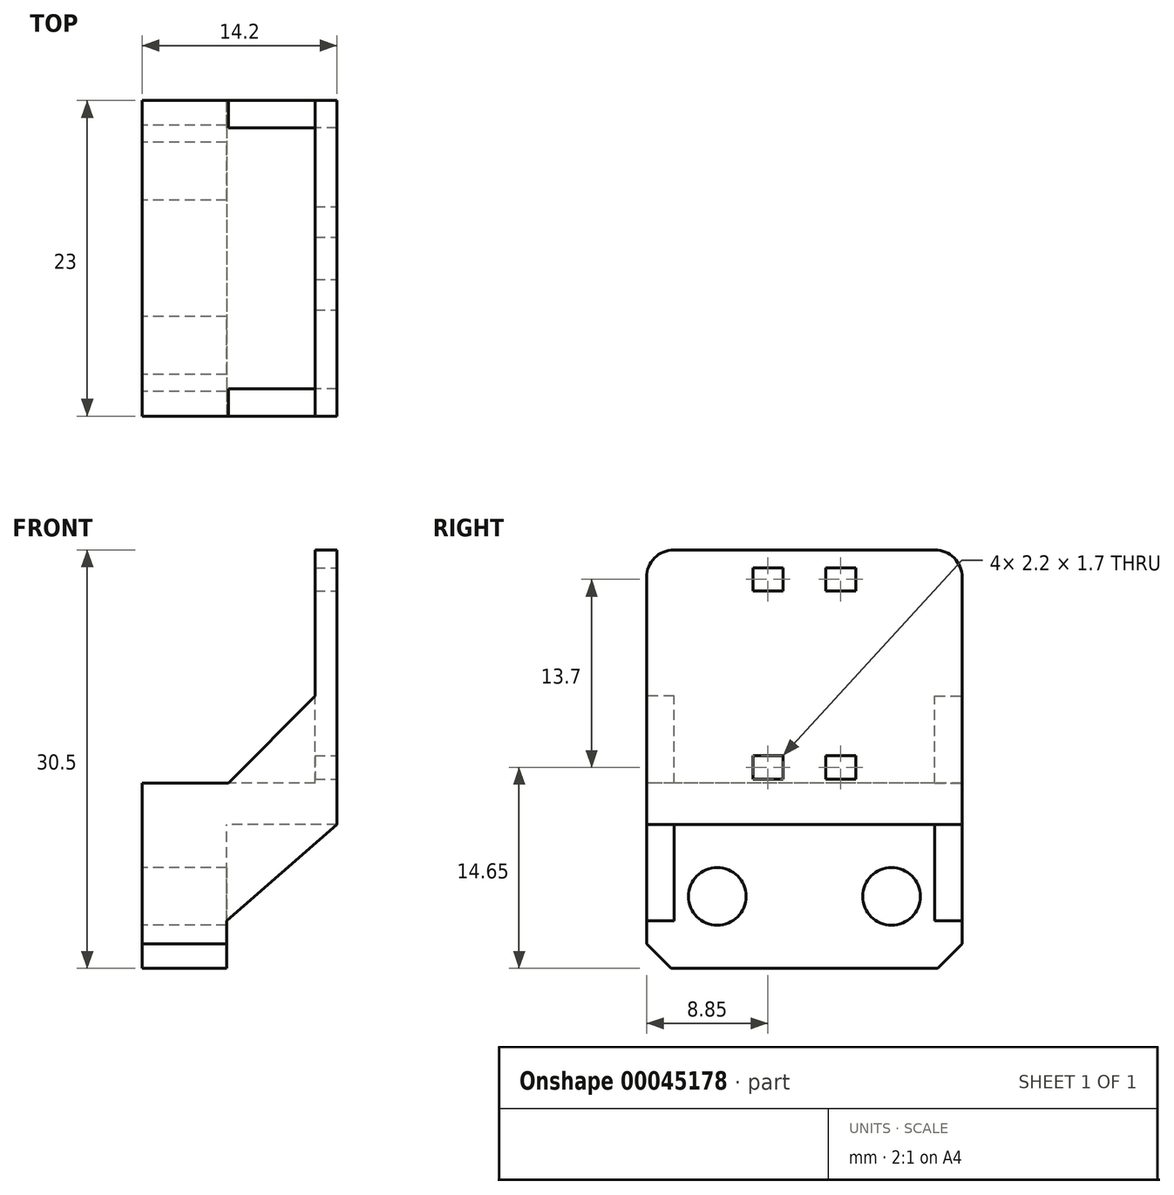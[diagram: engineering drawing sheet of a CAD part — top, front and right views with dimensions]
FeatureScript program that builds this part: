
annotation { "Feature Type Name" : "Feature", "Feature Type Description" : "" }
export const myFeature = defineFeature(function(context is Context, id is Id, definition is map)
    precondition{}
    {
        {
            var Q0;
            Q0=qCreatedBy(makeId("Right.planeOp"),FACE);
            var sketch = newSketch(context, id + "F0", { "sketchPlane" : qUnion([Q0])});
            skLineSegment(sketch, "E0.rect.bottom", {"start": v(9.71, -5.25) * mm, "end": v(-9.71, -5.25) * mm});
            skLineSegment(sketch, "E0.rect.top", {"start": v(9.71, 5.25) * mm, "end": v(-9.71, 5.25) * mm});
            skLineSegment(sketch, "E0.rect.left", {"start": v(11.5, -3.46) * mm, "end": v(11.5, 3.46) * mm});
            skLineSegment(sketch, "E0.rect.right", {"start": v(-11.5, -3.46) * mm, "end": v(-11.5, 3.46) * mm});
            skPoint(sketch, "E0.rect.middle", {"position": v(0, 0) * mm});
            skLineSegment(sketch, "E1", {"start": v(6.35, 5.25) * mm, "end": v(6.35, -5.25) * mm, "construction": true});
            skCircle(sketch, "E2", {"center": v(6.35, 0) * mm, "radius": 2.1 * mm});
            skCircle(sketch, "E3.MirrorC", {"center": v(-6.35, 0) * mm, "radius": 2.1 * mm});
            skLineSegment(sketch, "E4.MirrorCS", {"start": v(-9.71, -5.25) * mm, "end": v(-11.5, -3.46) * mm});
            skLineSegment(sketch, "E5.MirrorCS", {"start": v(9.71, -5.25) * mm, "end": v(11.5, -3.46) * mm});
            skPoint(sketch, "E6.orphan", {"position": v(-11.5, 5.25) * mm});
            skPoint(sketch, "E7.orphan", {"position": v(-11.5, -5.25) * mm});
            skPoint(sketch, "E8.orphan", {"position": v(11.5, 5.25) * mm});
            skPoint(sketch, "E9.orphan", {"position": v(11.5, -5.25) * mm});
            skLineSegment(sketch, "E10", {"start": v(11.5, 3.46) * mm, "end": v(11.5, 5.25) * mm});
            skLineSegment(sketch, "E11", {"start": v(11.5, 5.25) * mm, "end": v(9.71, 5.25) * mm});
            skLineSegment(sketch, "E12", {"start": v(-11.5, 3.46) * mm, "end": v(-11.5, 5.25) * mm});
            skLineSegment(sketch, "E13", {"start": v(-11.5, 5.25) * mm, "end": v(-9.71, 5.25) * mm});
            skSolve(sketch);
        }
        {
            var Q0;
            Q0=makeQuery(id+"F0.imprint","IMPRINT",FACE,{"disambiguationData":[TD([[makeQuery(id+"F0.imprint","IMPRINT",EDGE,{"derivedFrom":sQuery(id+"F0.wireOp",EDGE,"E0.rect.bottom")}),-1.0]])]});
            extrude(context, id + "F1", {"entities" : qUnion([Q0]), "depth" : 6.16 * mm});
        }
        {
            var Q0;
            Q0=makeQuery(id+"F1.opExtrude","CAP_FACE",FACE,{"disambiguationData":[OSD([sQuery(id+"F0.wireOp",EDGE,"E0.rect.bottom"),sQuery(id+"F0.wireOp",EDGE,"E0.rect.top"),sQuery(id+"F0.wireOp",EDGE,"E0.rect.left"),sQuery(id+"F0.wireOp",EDGE,"E0.rect.right"),sQuery(id+"F0.wireOp",EDGE,"E2"),sQuery(id+"F0.wireOp",EDGE,"E3.MirrorC"),sQuery(id+"F0.wireOp",EDGE,"E4.MirrorCS"),sQuery(id+"F0.wireOp",EDGE,"E5.MirrorCS"),sQuery(id+"F0.wireOp",EDGE,"E10"),sQuery(id+"F0.wireOp",EDGE,"E11"),sQuery(id+"F0.wireOp",EDGE,"E12"),sQuery(id+"F0.wireOp",EDGE,"E13")])],"isStart":true});
            var sketch = newSketch(context, id + "F2", { "sketchPlane" : qUnion([Q0])});
            skLineSegment(sketch, "E14.bottom", {"start": v(-11.5, 5.25) * mm, "end": v(11.5, 5.25) * mm});
            skLineSegment(sketch, "E14.top", {"start": v(-11.5, 8.25) * mm, "end": v(11.5, 8.25) * mm});
            skLineSegment(sketch, "E14.left", {"start": v(-11.5, 5.25) * mm, "end": v(-11.5, 8.25) * mm});
            skLineSegment(sketch, "E14.right", {"start": v(11.5, 5.25) * mm, "end": v(11.5, 8.25) * mm});
            skSolve(sketch);
        }
        {
            var Q0;
            Q0=qSketchRegion(id+"F2",true);
            extrude(context, id + "F3", {"entities" : qUnion([Q0]), "oppositeDirection" : true, "depth" : 14.2 * mm});
        }
        {
            var Q0;
            Q0=makeQuery(id+"F3.opExtrude","CAP_FACE",FACE,{"disambiguationData":[OSD([sQuery(id+"F2.wireOp",EDGE,"E14.bottom"),sQuery(id+"F2.wireOp",EDGE,"E14.top"),sQuery(id+"F2.wireOp",EDGE,"E14.left"),sQuery(id+"F2.wireOp",EDGE,"E14.right")])],"isStart":false});
            var sketch = newSketch(context, id + "F4", { "sketchPlane" : qUnion([Q0])});
            skLineSegment(sketch, "E15.bottom", {"start": v(-11.5, 5.25) * mm, "end": v(11.5, 5.25) * mm});
            skLineSegment(sketch, "E15.top", {"start": v(-11.5, 25.25) * mm, "end": v(11.5, 25.25) * mm});
            skLineSegment(sketch, "E15.left", {"start": v(-11.5, 5.25) * mm, "end": v(-11.5, 25.25) * mm});
            skLineSegment(sketch, "E15.right", {"start": v(11.5, 5.25) * mm, "end": v(11.5, 25.25) * mm});
            skLineSegment(sketch, "E16", {"start": v(-11.5, 16.25) * mm, "end": v(11.5, 16.25) * mm, "construction": true});
            skLineSegment(sketch, "E17.rect.bottom", {"start": v(3.75, 22.25) * mm, "end": v(-3.75, 22.25) * mm, "construction": true});
            skLineSegment(sketch, "E17.rect.top", {"start": v(3.75, 10.25) * mm, "end": v(-3.75, 10.25) * mm, "construction": true});
            skLineSegment(sketch, "E17.rect.left", {"start": v(3.75, 22.25) * mm, "end": v(3.75, 10.25) * mm, "construction": true});
            skLineSegment(sketch, "E17.rect.right", {"start": v(-3.75, 22.25) * mm, "end": v(-3.75, 10.25) * mm, "construction": true});
            skPoint(sketch, "E17.rect.middle", {"position": v(0, 16.25) * mm});
            skLineSegment(sketch, "E18.bottom", {"start": v(3.75, 22.25) * mm, "end": v(1.55, 22.25) * mm});
            skLineSegment(sketch, "E18.top", {"start": v(3.75, 23.95) * mm, "end": v(1.55, 23.95) * mm});
            skLineSegment(sketch, "E18.left", {"start": v(3.75, 22.25) * mm, "end": v(3.75, 23.95) * mm});
            skLineSegment(sketch, "E18.right", {"start": v(1.55, 22.25) * mm, "end": v(1.55, 23.95) * mm});
            skLineSegment(sketch, "E19.MirrorCS", {"start": v(-3.75, 23.95) * mm, "end": v(-1.55, 23.95) * mm});
            skLineSegment(sketch, "E20.MirrorCS", {"start": v(-1.55, 22.25) * mm, "end": v(-1.55, 23.95) * mm});
            skLineSegment(sketch, "E21.MirrorCS", {"start": v(-3.75, 22.25) * mm, "end": v(-1.55, 22.25) * mm});
            skLineSegment(sketch, "E22.MirrorCS", {"start": v(-3.75, 22.25) * mm, "end": v(-3.75, 23.95) * mm});
            skLineSegment(sketch, "E23.MirrorCS", {"start": v(3.75, 8.55) * mm, "end": v(1.55, 8.55) * mm});
            skLineSegment(sketch, "E24.MirrorCS", {"start": v(1.55, 10.25) * mm, "end": v(1.55, 8.55) * mm});
            skLineSegment(sketch, "E25.MirrorCS", {"start": v(3.75, 10.25) * mm, "end": v(1.55, 10.25) * mm});
            skLineSegment(sketch, "E26.MirrorCS", {"start": v(3.75, 10.25) * mm, "end": v(3.75, 8.55) * mm});
            skLineSegment(sketch, "E27.MirrorCS", {"start": v(-3.75, 8.55) * mm, "end": v(-1.55, 8.55) * mm});
            skLineSegment(sketch, "E28.MirrorCS", {"start": v(-3.75, 10.25) * mm, "end": v(-1.55, 10.25) * mm});
            skLineSegment(sketch, "E29.MirrorCS", {"start": v(-3.75, 10.25) * mm, "end": v(-3.75, 8.55) * mm});
            skLineSegment(sketch, "E30.MirrorCS", {"start": v(-1.55, 10.25) * mm, "end": v(-1.55, 8.55) * mm});
            skSolve(sketch);
        }
        {
            var Q0;
            Q0=qSketchRegion(id+"F4",true);
            extrude(context, id + "F5", {"entities" : qUnion([Q0]), "operationType" : NewBodyOperationType.ADD, "oppositeDirection" : true, "depth" : 1.6 * mm});
        }
        {
            var Q0;
            Q0=makeQuery(id+"F3.opExtrude","SWEPT_BODY",BODY,{"disambiguationData":[OSD([sQuery(id+"F2.wireOp",EDGE,"E14.bottom"),sQuery(id+"F2.wireOp",EDGE,"E14.top"),sQuery(id+"F2.wireOp",EDGE,"E14.left"),sQuery(id+"F2.wireOp",EDGE,"E14.right")])]});
            var Q1;
            Q1=makeQuery(id+"F1.opExtrude","SWEPT_BODY",BODY,{"disambiguationData":[OSD([sQuery(id+"F0.wireOp",EDGE,"E0.rect.bottom"),sQuery(id+"F0.wireOp",EDGE,"E0.rect.top"),sQuery(id+"F0.wireOp",EDGE,"E0.rect.left"),sQuery(id+"F0.wireOp",EDGE,"E0.rect.right"),sQuery(id+"F0.wireOp",EDGE,"E2"),sQuery(id+"F0.wireOp",EDGE,"E3.MirrorC"),sQuery(id+"F0.wireOp",EDGE,"E4.MirrorCS"),sQuery(id+"F0.wireOp",EDGE,"E5.MirrorCS"),sQuery(id+"F0.wireOp",EDGE,"E10"),sQuery(id+"F0.wireOp",EDGE,"E11"),sQuery(id+"F0.wireOp",EDGE,"E12"),sQuery(id+"F0.wireOp",EDGE,"E13")])]});
            booleanBodies(context, id + "F6", {"operationType" : BooleanOperationType.UNION, "tools" : qUnion([Q0, Q1])});
        }
        {
            var Q0;
            Q0=makeQuery(id+"F6.opBoolean","MERGE",FACE,{"derivedFrom":[makeQuery(id+"F1.opExtrude","SWEPT_FACE",FACE,{"disambiguationData":[OSD([sQuery(id+"F0.wireOp",EDGE,"E0.rect.left"),sQuery(id+"F0.wireOp",EDGE,"E10")])]}),makeQuery(id+"F5.boolean.opBoolean","MERGE",FACE,{"derivedFrom":[makeQuery(id+"F3.opExtrude","SWEPT_FACE",FACE,{"disambiguationData":[OSD([sQuery(id+"F2.wireOp",EDGE,"E14.left")])]}),makeQuery(id+"F5.opExtrude","SWEPT_FACE",FACE,{"disambiguationData":[OSD([sQuery(id+"F4.wireOp",EDGE,"E15.right")])]})]})]});
            var sketch = newSketch(context, id + "F7", { "sketchPlane" : qUnion([Q0])});
            skLineSegment(sketch, "E31", {"start": v(-12.6, 14.6) * mm, "end": v(-6.3, 8.25) * mm});
            skLineSegment(sketch, "E32", {"start": v(-6.3, 8.25) * mm, "end": v(-12.6, 8.25) * mm});
            skLineSegment(sketch, "E33", {"start": v(-12.6, 8.25) * mm, "end": v(-12.6, 14.6) * mm});
            skLineSegment(sketch, "E34", {"start": v(-14.2, 5.25) * mm, "end": v(-6.16, -1.77) * mm});
            skLineSegment(sketch, "E35", {"start": v(-6.16, -1.77) * mm, "end": v(-6.16, 5.25) * mm});
            skLineSegment(sketch, "E36", {"start": v(-6.16, 5.25) * mm, "end": v(-14.2, 5.25) * mm});
            skSolve(sketch);
        }
        {
            var Q0;
            Q0=qSketchRegion(id+"F7",true);
            extrude(context, id + "F8", {"entities" : qUnion([Q0]), "oppositeDirection" : true, "depth" : 2 * mm});
        }
        {
            var Q0;
            Q0=qCreatedBy(makeId("Front.planeOp"),FACE);
            cPlane(context, id + "F9", {"entities" : qUnion([Q0]), "cplaneType" : CPlaneType.OFFSET, "offset" : 0 * mm, "width" : 150 * mm, "height" : 150 * mm});
        }
        {
            var Q0;
            Q0=makeQuery(id+"F8.opExtrude","SWEPT_BODY",BODY,{"disambiguationData":[OSD([sQuery(id+"F7.wireOp",EDGE,"E31"),sQuery(id+"F7.wireOp",EDGE,"E32"),sQuery(id+"F7.wireOp",EDGE,"E33")])]});
            var Q1;
            Q1=qCreatedBy(id+"F9.planeOp",FACE);
            mirror(context, id + "F10", {"operationType" : NewBodyOperationType.ADD, "entities" : qUnion([Q0]), "mirrorPlane" : qUnion([Q1])});
        }
        {
            var Q0;
            Q0=makeQuery(id+"F8.opExtrude","SWEPT_BODY",BODY,{"disambiguationData":[OSD([sQuery(id+"F7.wireOp",EDGE,"E34"),sQuery(id+"F7.wireOp",EDGE,"E35"),sQuery(id+"F7.wireOp",EDGE,"E36")])]});
            var Q1;
            Q1=qCreatedBy(id+"F9.planeOp",FACE);
            mirror(context, id + "F11", {"operationType" : NewBodyOperationType.ADD, "entities" : qUnion([Q0]), "mirrorPlane" : qUnion([Q1])});
        }
        {
            var Q0;
            Q0=makeQuery(id+"F5.opExtrude","SWEPT_EDGE",EDGE,{"disambiguationData":[OSD([sQuery(id+"F4.wireOp",EDGE,"E15.top"),sQuery(id+"F4.wireOp",EDGE,"E15.right")])]});
            var Q1;
            Q1=makeQuery(id+"F5.opExtrude","SWEPT_EDGE",EDGE,{"disambiguationData":[OSD([sQuery(id+"F4.wireOp",EDGE,"E15.top"),sQuery(id+"F4.wireOp",EDGE,"E15.left")])]});
            fillet(context, id + "F12", {"entities" : qUnion([Q0, Q1]), "radius" : 2 * mm, "tangentPropagation" : true, "allowEdgeOverflow" : false});
        }
    });
